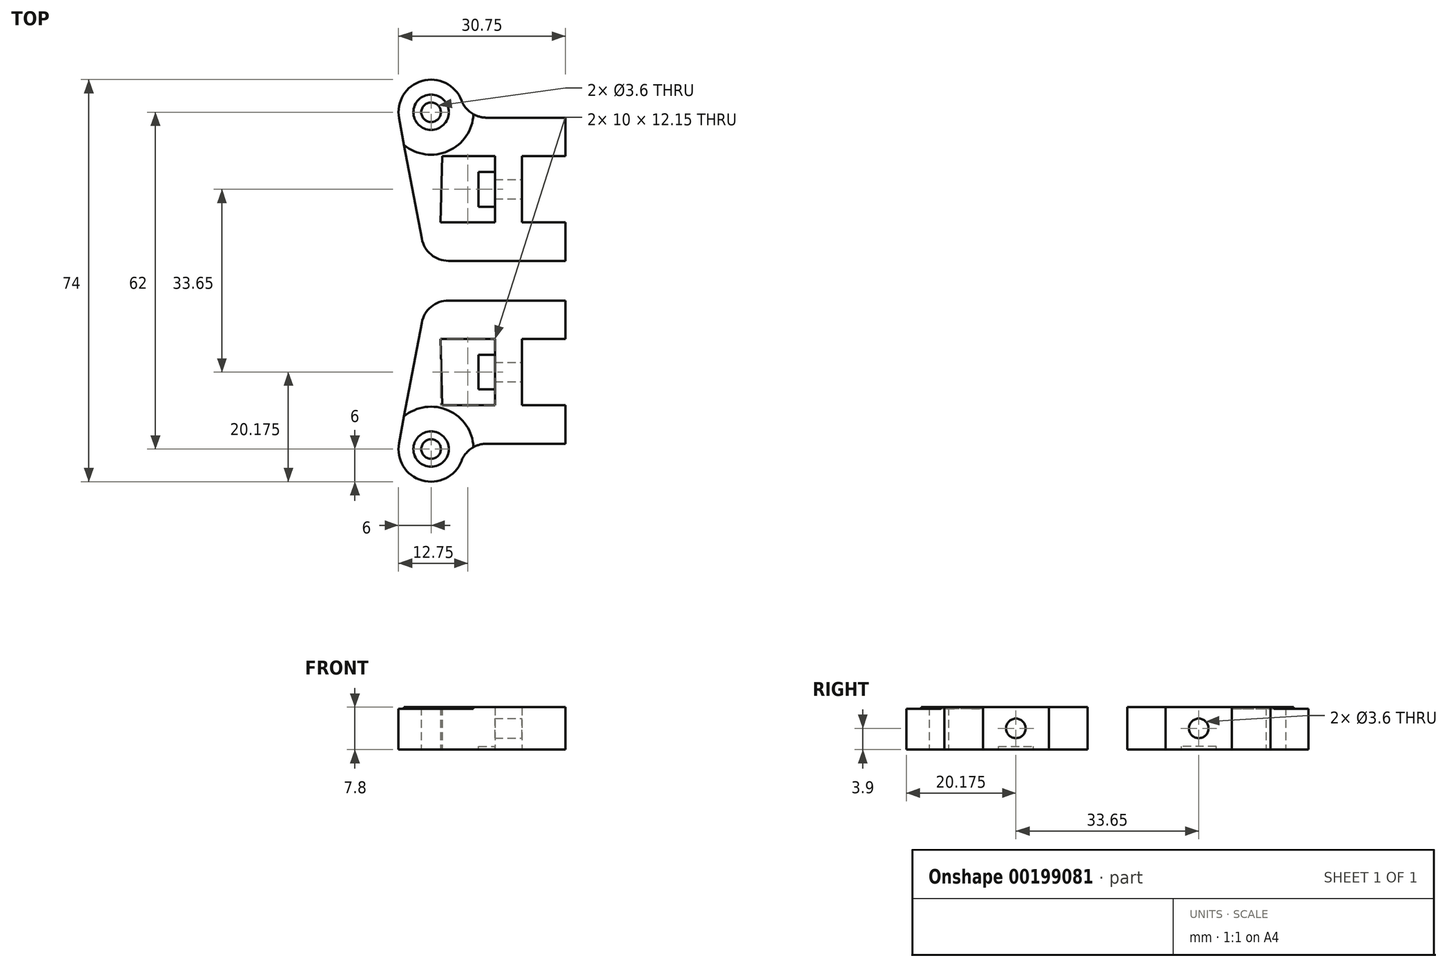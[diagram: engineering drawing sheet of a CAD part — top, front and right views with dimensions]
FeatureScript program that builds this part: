
annotation { "Feature Type Name" : "Feature", "Feature Type Description" : "" }
export const myFeature = defineFeature(function(context is Context, id is Id, definition is map)
    precondition{}
    {
        {
            var Q0;
            Q0=qCreatedBy(makeId("Top.planeOp"),FACE);
            var sketch = newSketch(context, id + "F0", { "sketchPlane" : qUnion([Q0])});
            skLineSegment(sketch, "E0.bottom", {"start": v(8.5, 0) * mm, "end": v(23, 0) * mm});
            skLineSegment(sketch, "E0.top", {"start": v(0.32, -7.1) * mm, "end": v(10, -7.1) * mm});
            skLineSegment(sketch, "E0.right", {"start": v(23, 0) * mm, "end": v(23, -7.1) * mm});
            skLineSegment(sketch, "E1.bottom", {"start": v(0, -19.25) * mm, "end": v(10, -19.25) * mm});
            skLineSegment(sketch, "E1.top", {"start": v(-0.19, -26.35) * mm, "end": v(23, -26.35) * mm});
            skLineSegment(sketch, "E1.right", {"start": v(23, -19.25) * mm, "end": v(23, -26.35) * mm});
            skLineSegment(sketch, "E2.left", {"start": v(10, -7.1) * mm, "end": v(10, -19.25) * mm});
            skLineSegment(sketch, "E2.right", {"start": v(15, -7.1) * mm, "end": v(15, -19.25) * mm});
            skCircle(sketch, "E3", {"center": v(-1.75, 1) * mm, "radius": 1.8 * mm});
            skArc(sketch, "E4", {"start": v(3.84, 3.18) * mm, "mid": v(-3.4, 6.77) * mm, "end": v(-7.65, -0.11) * mm});
            skLineSegment(sketch, "E5.top", {"start": v(-0.19, -26.35) * mm, "end": v(-2.69, -26.35) * mm});
            skLineSegment(sketch, "E6.trimOffspring", {"start": v(15, -7.1) * mm, "end": v(23, -7.1) * mm});
            skLineSegment(sketch, "E7.trimOffspring", {"start": v(15, -19.25) * mm, "end": v(23, -19.25) * mm});
            skLineSegment(sketch, "E8.trimOffspring", {"start": v(0.32, -7.1) * mm, "end": v(0, -19.25) * mm});
            skPoint(sketch, "E9.orphan", {"position": v(0, 0) * mm});
            skArc(sketch, "E10.filletArc", {"start": v(3.84, 3.18) * mm, "mid": v(5.68, 0.87) * mm, "end": v(8.5, 0) * mm});
            skLineSegment(sketch, "E11", {"start": v(-2.69, -26.35) * mm, "end": v(-7.65, -0.11) * mm});
            skPoint(sketch, "E12.orphan", {"position": v(0, -26.35) * mm});
            skSolve(sketch);
        }
        {
            var Q0;
            Q0=makeQuery(id+"F0.imprint","IMPRINT",FACE,{"disambiguationData":[TD([[makeQuery(id+"F0.imprint","IMPRINT",EDGE,{"derivedFrom":sQuery(id+"F0.wireOp",EDGE,"E0.bottom")}),-1.0]])]});
            extrude(context, id + "F1", {"entities" : qUnion([Q0]), "depth" : 7.8 * mm});
        }
        {
            var Q0;
            Q0=makeQuery(id+"F1.opExtrude","SWEPT_EDGE",EDGE,{"disambiguationData":[OSD([sQuery(id+"F0.wireOp",EDGE,"E5.top"),sQuery(id+"F0.wireOp",EDGE,"E11")])]});
            fillet(context, id + "F2", {"entities" : qUnion([Q0]), "radius" : 5 * mm, "tangentPropagation" : true, "allowEdgeOverflow" : false});
        }
        {
            var Q0;
            Q0=makeQuery(id+"F1.opExtrude","SWEPT_FACE",FACE,{"disambiguationData":[OSD([sQuery(id+"F0.wireOp",EDGE,"E2.right")])]});
            var sketch = newSketch(context, id + "F3", { "sketchPlane" : qUnion([Q0])});
            skCircle(sketch, "E13", {"center": v(-13.18, 3.9) * mm, "radius": 1.8 * mm});
            skSolve(sketch);
        }
        {
            var Q0;
            Q0 = qSketchRegion(id + "F3", true);
            extrude(context, id + "F4", {"entities" : qUnion([Q0]), "operationType" : NewBodyOperationType.REMOVE, "oppositeDirection" : true, "depth" : 6 * mm});
        }
        {
            var Q0;
            Q0=makeQuery(id+"F1.opExtrude","SWEPT_FACE",FACE,{"disambiguationData":[OSD([sQuery(id+"F0.wireOp",EDGE,"E2.left")])]});
            var sketch = newSketch(context, id + "F5", { "sketchPlane" : qUnion([Q0])});
            skLineSegment(sketch, "E14.bottom", {"start": v(9.97, 0) * mm, "end": v(16.38, 0) * mm});
            skLineSegment(sketch, "E14.top", {"start": v(9.97, 6.4) * mm, "end": v(16.38, 6.4) * mm});
            skLineSegment(sketch, "E14.left", {"start": v(9.97, 0) * mm, "end": v(9.97, 6.4) * mm});
            skLineSegment(sketch, "E14.right", {"start": v(16.38, 0) * mm, "end": v(16.38, 6.4) * mm});
            skLineSegment(sketch, "E15.0.0", {"start": v(7.1, 0) * mm, "end": v(19.25, 0) * mm});
            skLineSegment(sketch, "E15.0.1", {"start": v(19.25, 0) * mm, "end": v(19.25, 7.8) * mm});
            skLineSegment(sketch, "E15.0.2", {"start": v(19.25, 7.8) * mm, "end": v(7.1, 7.8) * mm});
            skLineSegment(sketch, "E15.0.3", {"start": v(7.1, 7.8) * mm, "end": v(7.1, 0) * mm});
            skCircle(sketch, "E16.0", {"center": v(13.17, 3.9) * mm, "radius": 1.8 * mm});
            skLineSegment(sketch, "E17", {"start": v(13.17, 3.9) * mm, "end": v(13.17, 6.4) * mm});
            skPoint(sketch, "E17.endSnap0", {"position": v(13.17, 6.4) * mm});
            skLineSegment(sketch, "E18.bottom", {"start": v(9.38, 0) * mm, "end": v(9.97, 0) * mm});
            skLineSegment(sketch, "E18.top", {"start": v(9.38, 6.4) * mm, "end": v(9.97, 6.4) * mm});
            skLineSegment(sketch, "E18.left", {"start": v(9.38, 0) * mm, "end": v(9.38, 6.4) * mm});
            skLineSegment(sketch, "E19.bottom", {"start": v(16.38, 0) * mm, "end": v(16.98, 0) * mm});
            skLineSegment(sketch, "E19.top", {"start": v(16.38, 6.4) * mm, "end": v(16.98, 6.4) * mm});
            skLineSegment(sketch, "E19.right", {"start": v(16.98, 0) * mm, "end": v(16.98, 6.4) * mm});
            skLineSegment(sketch, "E20.top", {"start": v(9.97, 0.6) * mm, "end": v(16.38, 0.6) * mm});
            skLineSegment(sketch, "E20.left", {"start": v(9.97, 0) * mm, "end": v(9.97, 0.6) * mm});
            skLineSegment(sketch, "E20.right", {"start": v(16.38, 0) * mm, "end": v(16.38, 0.6) * mm});
            skSolve(sketch);
        }
        {
            var Q0;
            Q0=makeQuery(id+"F5.imprint","IMPRINT",FACE,{"disambiguationData":[TD([[makeQuery(id+"F5.imprint","IMPRINT",EDGE,{"derivedFrom":sQuery(id+"F5.wireOp",EDGE,"E18.bottom")}),1.0]])]});
            var Q1;
            Q1=makeQuery(id+"F5.imprint","IMPRINT",FACE,{"disambiguationData":[TD([[makeQuery(id+"F5.imprint","IMPRINT",EDGE,{"derivedFrom":sQuery(id+"F5.wireOp",EDGE,"E19.bottom")}),1.0]])]});
            var Q2;
            Q2=makeQuery(id+"F5.imprint","IMPRINT",FACE,{"disambiguationData":[TD([[makeQuery(id+"F5.imprint","IMPRINT",EDGE,{"derivedFrom":sQuery(id+"F5.wireOp",EDGE,"E14.bottom")}),1.0]])]});
            extrude(context, id + "F6", {"entities" : qUnion([Q0, Q1, Q2]), "operationType" : NewBodyOperationType.ADD, "depth" : 3 * mm});
        }
        {
            var Q0;
            Q0=qCreatedBy(makeId("Front.planeOp"),FACE);
            cPlane(context, id + "F7", {"entities" : qUnion([Q0]), "cplaneType" : CPlaneType.OFFSET, "offset" : 30 * mm, "width" : 150 * mm, "height" : 150 * mm});
        }
        {
            var Q0;
            Q0=makeQuery(id+"F1.opExtrude","SWEPT_BODY",BODY,{"disambiguationData":[OSD([sQuery(id+"F0.wireOp",EDGE,"E0.bottom"),sQuery(id+"F0.wireOp",EDGE,"E0.top"),sQuery(id+"F0.wireOp",EDGE,"E0.right"),sQuery(id+"F0.wireOp",EDGE,"E1.bottom"),sQuery(id+"F0.wireOp",EDGE,"E1.top"),sQuery(id+"F0.wireOp",EDGE,"E1.right"),sQuery(id+"F0.wireOp",EDGE,"E2.left"),sQuery(id+"F0.wireOp",EDGE,"E2.right"),sQuery(id+"F0.wireOp",EDGE,"E3"),sQuery(id+"F0.wireOp",EDGE,"E4"),sQuery(id+"F0.wireOp",EDGE,"E5.top"),sQuery(id+"F0.wireOp",EDGE,"E6.trimOffspring"),sQuery(id+"F0.wireOp",EDGE,"E7.trimOffspring"),sQuery(id+"F0.wireOp",EDGE,"E8.trimOffspring"),sQuery(id+"F0.wireOp",EDGE,"E10.filletArc"),sQuery(id+"F0.wireOp",EDGE,"E11")])]});
            var Q1;
            Q1=qCreatedBy(id+"F7.planeOp",FACE);
            mirror(context, id + "F8", {"entities" : qUnion([Q0]), "mirrorPlane" : qUnion([Q1])});
        }
        {
            var Q0;
            Q0=makeQuery(id+"F1.opExtrude","CAP_FACE",FACE,{"disambiguationData":[OSD([sQuery(id+"F0.wireOp",EDGE,"E0.bottom"),sQuery(id+"F0.wireOp",EDGE,"E0.top"),sQuery(id+"F0.wireOp",EDGE,"E0.right"),sQuery(id+"F0.wireOp",EDGE,"E1.bottom"),sQuery(id+"F0.wireOp",EDGE,"E1.top"),sQuery(id+"F0.wireOp",EDGE,"E1.right"),sQuery(id+"F0.wireOp",EDGE,"E2.left"),sQuery(id+"F0.wireOp",EDGE,"E2.right"),sQuery(id+"F0.wireOp",EDGE,"E3"),sQuery(id+"F0.wireOp",EDGE,"E4"),sQuery(id+"F0.wireOp",EDGE,"E5.top"),sQuery(id+"F0.wireOp",EDGE,"E6.trimOffspring"),sQuery(id+"F0.wireOp",EDGE,"E7.trimOffspring"),sQuery(id+"F0.wireOp",EDGE,"E8.trimOffspring"),sQuery(id+"F0.wireOp",EDGE,"E10.filletArc"),sQuery(id+"F0.wireOp",EDGE,"E11")])],"isStart":false});
            var sketch = newSketch(context, id + "F9", { "sketchPlane" : qUnion([Q0])});
            skCircle(sketch, "E21.0", {"center": v(-1.75, 1) * mm, "radius": 1.8 * mm});
            skCircle(sketch, "E22", {"center": v(-1.75, 1) * mm, "radius": 3.25 * mm});
            skCircle(sketch, "E23", {"center": v(-1.75, 1) * mm, "radius": 7.8 * mm});
            skSolve(sketch);
        }
        {
            var Q0;
            Q0=makeQuery(id+"F9.imprint","IMPRINT",FACE,{"disambiguationData":[TD([[makeQuery(id+"F9.imprint","IMPRINT",EDGE,{"derivedFrom":sQuery(id+"F9.wireOp",EDGE,"E22")}),-1.0]])]});
            extrude(context, id + "F10", {"entities" : qUnion([Q0]), "operationType" : NewBodyOperationType.REMOVE, "oppositeDirection" : true, "depth" : 0.3 * mm});
        }
        {
            var Q0;
            Q0=makeQuery(id+"F8.opPattern","COPY",BODY,{"derivedFrom":makeQuery(id+"F1.opExtrude","SWEPT_BODY",BODY,{"disambiguationData":[OSD([sQuery(id+"F0.wireOp",EDGE,"E0.bottom"),sQuery(id+"F0.wireOp",EDGE,"E0.top"),sQuery(id+"F0.wireOp",EDGE,"E0.right"),sQuery(id+"F0.wireOp",EDGE,"E1.bottom"),sQuery(id+"F0.wireOp",EDGE,"E1.top"),sQuery(id+"F0.wireOp",EDGE,"E1.right"),sQuery(id+"F0.wireOp",EDGE,"E2.left"),sQuery(id+"F0.wireOp",EDGE,"E2.right"),sQuery(id+"F0.wireOp",EDGE,"E3"),sQuery(id+"F0.wireOp",EDGE,"E4"),sQuery(id+"F0.wireOp",EDGE,"E5.top"),sQuery(id+"F0.wireOp",EDGE,"E6.trimOffspring"),sQuery(id+"F0.wireOp",EDGE,"E7.trimOffspring"),sQuery(id+"F0.wireOp",EDGE,"E8.trimOffspring"),sQuery(id+"F0.wireOp",EDGE,"E10.filletArc"),sQuery(id+"F0.wireOp",EDGE,"E11")])]}),"instanceName":"1"});
            deleteBodies(context, id + "F11", {"entities" : qUnion([Q0])});
        }
        {
            var Q0;
            Q0=makeQuery(id+"F1.opExtrude","SWEPT_BODY",BODY,{"disambiguationData":[OSD([sQuery(id+"F0.wireOp",EDGE,"E0.bottom"),sQuery(id+"F0.wireOp",EDGE,"E0.top"),sQuery(id+"F0.wireOp",EDGE,"E0.right"),sQuery(id+"F0.wireOp",EDGE,"E1.bottom"),sQuery(id+"F0.wireOp",EDGE,"E1.top"),sQuery(id+"F0.wireOp",EDGE,"E1.right"),sQuery(id+"F0.wireOp",EDGE,"E2.left"),sQuery(id+"F0.wireOp",EDGE,"E2.right"),sQuery(id+"F0.wireOp",EDGE,"E3"),sQuery(id+"F0.wireOp",EDGE,"E4"),sQuery(id+"F0.wireOp",EDGE,"E5.top"),sQuery(id+"F0.wireOp",EDGE,"E6.trimOffspring"),sQuery(id+"F0.wireOp",EDGE,"E7.trimOffspring"),sQuery(id+"F0.wireOp",EDGE,"E8.trimOffspring"),sQuery(id+"F0.wireOp",EDGE,"E10.filletArc"),sQuery(id+"F0.wireOp",EDGE,"E11")])]});
            var Q1;
            Q1=qCreatedBy(id+"F7.planeOp",FACE);
            mirror(context, id + "F12", {"entities" : qUnion([Q0]), "mirrorPlane" : qUnion([Q1])});
        }
    });
